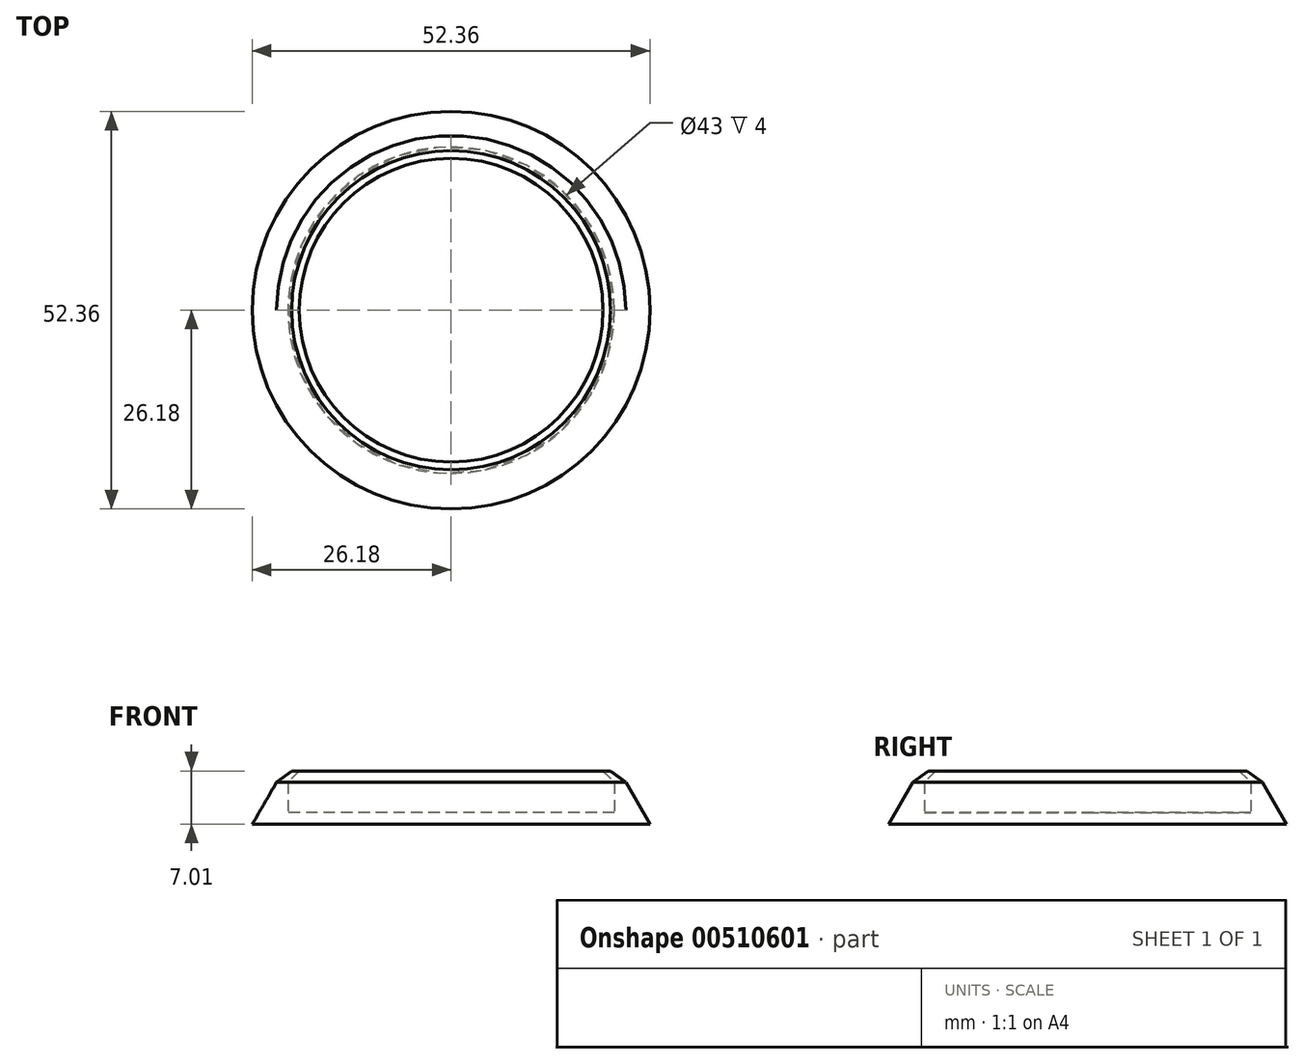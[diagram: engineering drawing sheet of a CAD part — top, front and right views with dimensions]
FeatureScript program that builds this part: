
annotation { "Feature Type Name" : "Feature", "Feature Type Description" : "" }
export const myFeature = defineFeature(function(context is Context, id is Id, definition is map)
    precondition{}
    {
        {
            var Q0;
            Q0=qCreatedBy(makeId("Top.planeOp"),FACE);
            var sketch = newSketch(context, id + "F0", { "sketchPlane" : qUnion([Q0])});
            skCircle(sketch, "E0", {"center": v(0, 0) * mm, "radius": 23 * mm});
            skSolve(sketch);
        }
        {
            var Q0;
            Q0 = qSketchRegion(id + "F0", true);
            extrude(context, id + "F1", {"entities" : qUnion([Q0]), "depth" : 5.5 * mm});
        }
        {
            var Q0;
            Q0=makeQuery(id+"F1.opExtrude","CAP_FACE",FACE,{"disambiguationData":[OSD([sQuery(id+"F0.wireOp",EDGE,"E0")])],"isStart":false});
            shell(context, id + "F2", {"entities" : qUnion([Q0]), "thickness" : 1.5 * mm});
        }
        {
            var Q0;
            Q0=qCreatedBy(makeId("Front.planeOp"),FACE);
            var sketch = newSketch(context, id + "F3", { "sketchPlane" : qUnion([Q0])});
            skLineSegment(sketch, "E1", {"start": v(0, 0) * mm, "end": v(0, 26.13) * mm, "construction": true});
            skLineSegment(sketch, "E2", {"start": v(0, 5.5) * mm, "end": v(23, 5.5) * mm, "construction": true});
            skLineSegment(sketch, "E3", {"start": v(0, 0) * mm, "end": v(23, 0) * mm, "construction": true});
            skLineSegment(sketch, "E4", {"start": v(23, 5.5) * mm, "end": v(23, 0) * mm});
            skLineSegment(sketch, "E5", {"start": v(23, 0) * mm, "end": v(26.18, 0) * mm});
            skLineSegment(sketch, "E6", {"start": v(26.18, 0) * mm, "end": v(23, 5.5) * mm});
            skSolve(sketch);
        }
        {
            var Q0;
            Q0 = qSketchRegion(id + "F3", true);
            var Q1;
            Q1=sQuery(id+"F3.wireOp",EDGE,"E1");
            revolve(context, id + "F4", {"operationType" : NewBodyOperationType.ADD, "entities" : qUnion([Q0]), "axis" : qUnion([Q1]), "revolveType" : RevolveType.FULL});
        }
        {
            var Q0;
            Q0=qCreatedBy(makeId("Front.planeOp"),FACE);
            var sketch = newSketch(context, id + "F5", { "sketchPlane" : qUnion([Q0])});
            skLineSegment(sketch, "E7", {"start": v(-20, 7.01) * mm, "end": v(-21, 7.01) * mm});
            skLineSegment(sketch, "E8", {"start": v(0, 27.92) * mm, "end": v(0, 0) * mm, "construction": true});
            skLineSegment(sketch, "E9", {"start": v(-23, 5.5) * mm, "end": v(-21, 7.01) * mm});
            skLineSegment(sketch, "E10", {"start": v(-20, 7.01) * mm, "end": v(-21.5, 5.5) * mm});
            skLineSegment(sketch, "E11", {"start": v(-23, 5.5) * mm, "end": v(-21.5, 5.5) * mm});
            skSolve(sketch);
        }
        {
            var Q0;
            Q0 = qSketchRegion(id + "F5", true);
            var Q1;
            Q1=sQuery(id+"F5.wireOp",EDGE,"E8");
            revolve(context, id + "F6", {"operationType" : NewBodyOperationType.ADD, "entities" : qUnion([Q0]), "axis" : qUnion([Q1]), "revolveType" : RevolveType.FULL});
        }
    });
